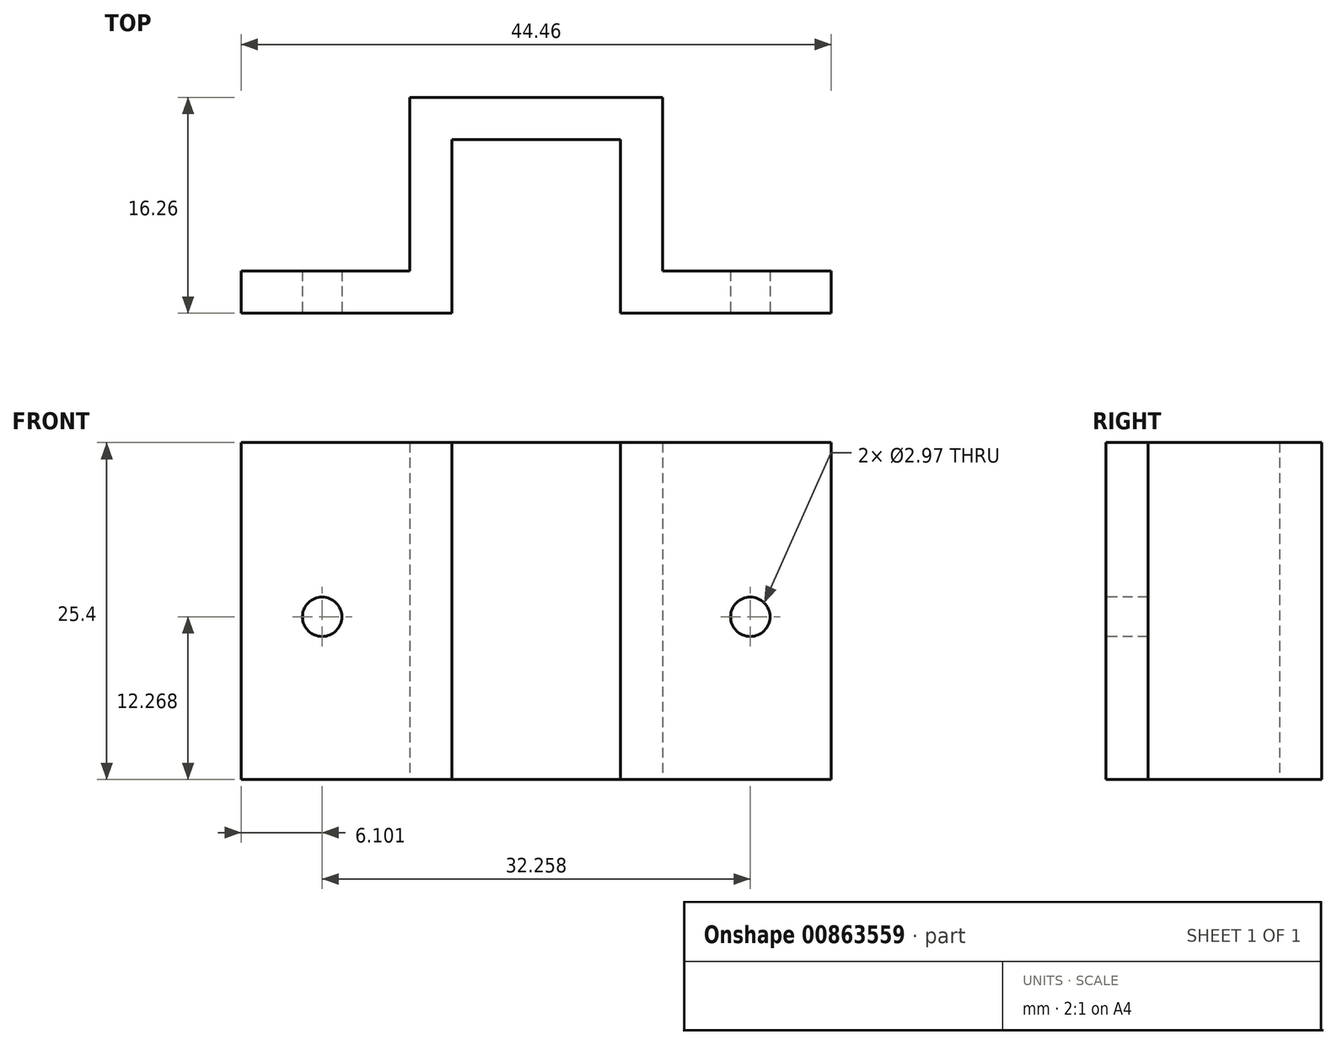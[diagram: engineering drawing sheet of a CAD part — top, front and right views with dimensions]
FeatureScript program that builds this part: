
annotation { "Feature Type Name" : "Feature", "Feature Type Description" : "" }
export const myFeature = defineFeature(function(context is Context, id is Id, definition is map)
    precondition{}
    {
        {
            var Q0;
            Q0=qCreatedBy(makeId("Top.planeOp"),FACE);
            var sketch = newSketch(context, id + "F0", { "sketchPlane" : qUnion([Q0])});
            skLineSegment(sketch, "E0", {"start": v(-22.23, 0) * mm, "end": v(-22.23, 3.17) * mm});
            skLineSegment(sketch, "E1", {"start": v(-22.23, 3.17) * mm, "end": v(-9.53, 3.17) * mm});
            skLineSegment(sketch, "E2", {"start": v(-9.53, 3.17) * mm, "end": v(-9.53, 16.26) * mm});
            skLineSegment(sketch, "E3", {"start": v(-9.53, 16.26) * mm, "end": v(9.52, 16.26) * mm});
            skLineSegment(sketch, "E4", {"start": v(9.52, 16.26) * mm, "end": v(9.52, 3.17) * mm});
            skLineSegment(sketch, "E5", {"start": v(9.52, 3.17) * mm, "end": v(22.23, 3.18) * mm});
            skLineSegment(sketch, "E6", {"start": v(22.23, 3.17) * mm, "end": v(22.23, 0) * mm});
            skLineSegment(sketch, "E7", {"start": v(22.23, 0) * mm, "end": v(6.35, 0) * mm});
            skLineSegment(sketch, "E8", {"start": v(6.35, 0) * mm, "end": v(6.35, 13.08) * mm});
            skLineSegment(sketch, "E9", {"start": v(6.35, 13.08) * mm, "end": v(-6.35, 13.08) * mm});
            skLineSegment(sketch, "E10", {"start": v(-6.35, 13.08) * mm, "end": v(-6.35, 0) * mm});
            skLineSegment(sketch, "E11", {"start": v(-6.35, 0) * mm, "end": v(-22.23, 0) * mm});
            skSolve(sketch);
        }
        {
            var Q0;
            Q0 = qSketchRegion(id + "F0", true);
            extrude(context, id + "F1", {"entities" : qUnion([Q0]), "depth" : 25.4 * mm, "offsetDistance" : 25.4 * mm});
        }
        {
            var Q0;
            Q0=makeQuery(id+"F1.opExtrude","SWEPT_FACE",FACE,{"disambiguationData":[OSD([sQuery(id+"F0.wireOp",EDGE,"E11")])]});
            var sketch = newSketch(context, id + "F2", { "sketchPlane" : qUnion([Q0])});
            skCircle(sketch, "E12", {"center": v(-16.13, 12.27) * mm, "radius": 1.49 * mm});
            skCircle(sketch, "E13", {"center": v(16.13, 12.27) * mm, "radius": 1.49 * mm});
            skSolve(sketch);
        }
        {
            var Q0;
            Q0 = qSketchRegion(id + "F2", true);
            extrude(context, id + "F3", {"entities" : qUnion([Q0]), "operationType" : NewBodyOperationType.REMOVE, "endBound" : BoundingType.THROUGH_ALL, "oppositeDirection" : true, "depth" : 25.4 * mm, "offsetDistance" : 25.4 * mm});
        }
    });
